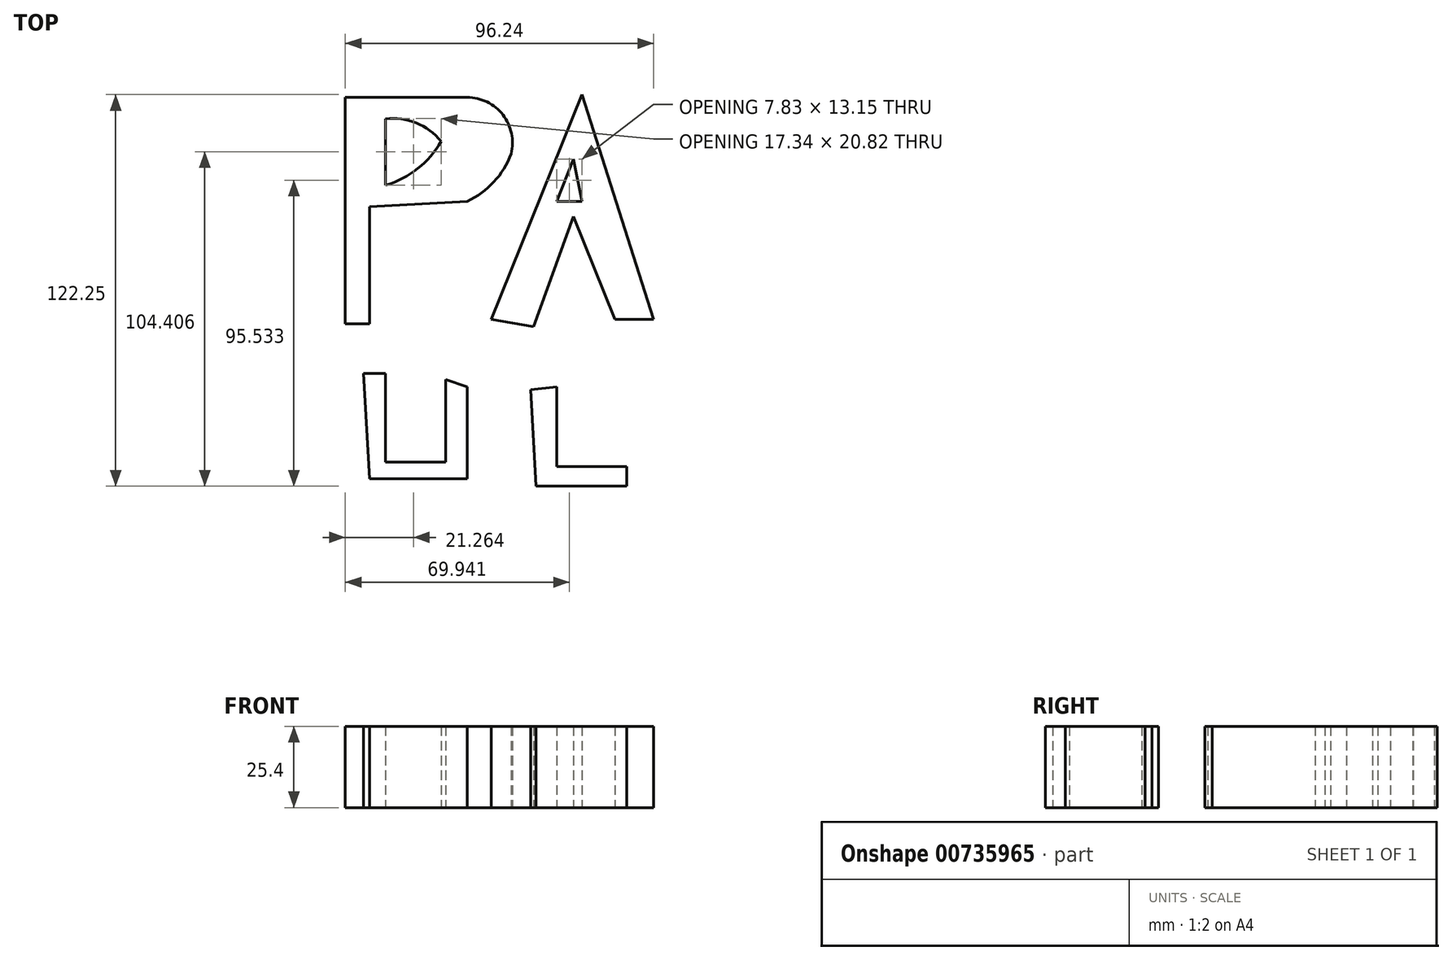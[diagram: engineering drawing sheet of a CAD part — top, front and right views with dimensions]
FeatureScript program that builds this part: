
annotation { "Feature Type Name" : "Feature", "Feature Type Description" : "" }
export const myFeature = defineFeature(function(context is Context, id is Id, definition is map)
    precondition{}
    {
        {
            var Q0;
            Q0=qCreatedBy(makeId("Top.planeOp"),FACE);
            var sketch = newSketch(context, id + "F0", { "sketchPlane" : qUnion([Q0])});
            skLineSegment(sketch, "E0", {"start": v(-71.2, 45.74) * mm, "end": v(-71.2, -25.04) * mm});
            skLineSegment(sketch, "E1", {"start": v(-71.2, -25.04) * mm, "end": v(-63.64, -25.04) * mm});
            skLineSegment(sketch, "E2", {"start": v(-63.64, -25.04) * mm, "end": v(-63.64, 11.6) * mm});
            skLineSegment(sketch, "E3", {"start": v(-71.2, 45.74) * mm, "end": v(-33.15, 45.74) * mm});
            skArc(sketch, "E4", {"start": v(-19.44, 28.12) * mm, "mid": v(-21.99, 40.28) * mm, "end": v(-33.15, 45.74) * mm});
            skArc(sketch, "E5", {"start": v(-33.15, 13.29) * mm, "mid": v(-24.8, 19.32) * mm, "end": v(-19.44, 28.12) * mm});
            skLineSegment(sketch, "E6", {"start": v(-63.64, 11.6) * mm, "end": v(-33.15, 13.29) * mm});
            skLineSegment(sketch, "E7", {"start": v(2.66, 46.58) * mm, "end": v(-25.6, -23.64) * mm});
            skLineSegment(sketch, "E8", {"start": v(-25.6, -23.64) * mm, "end": v(-12.45, -25.88) * mm});
            skLineSegment(sketch, "E9", {"start": v(-12.45, -25.88) * mm, "end": v(0, 8.53) * mm});
            skLineSegment(sketch, "E10", {"start": v(0, 8.53) * mm, "end": v(13, -23.64) * mm});
            skLineSegment(sketch, "E11", {"start": v(13, -23.64) * mm, "end": v(25.04, -23.64) * mm});
            skLineSegment(sketch, "E12", {"start": v(25.04, -23.64) * mm, "end": v(2.66, 46.58) * mm});
            skLineSegment(sketch, "E13", {"start": v(0, 26.44) * mm, "end": v(-5.18, 13.29) * mm});
            skLineSegment(sketch, "E14", {"start": v(-5.18, 13.29) * mm, "end": v(2.66, 13.29) * mm});
            skLineSegment(sketch, "E15", {"start": v(2.66, 13.29) * mm, "end": v(0, 26.44) * mm});
            skLineSegment(sketch, "E16", {"start": v(-58.6, -40.42) * mm, "end": v(-58.6, -68.12) * mm});
            skLineSegment(sketch, "E17", {"start": v(-58.6, -68.12) * mm, "end": v(-39.87, -68.12) * mm});
            skLineSegment(sketch, "E18", {"start": v(-39.87, -68.12) * mm, "end": v(-39.87, -42.38) * mm});
            skLineSegment(sketch, "E19", {"start": v(-5.18, -44.62) * mm, "end": v(-5.18, -69.52) * mm});
            skLineSegment(sketch, "E20", {"start": v(-5.18, -69.52) * mm, "end": v(16.65, -69.52) * mm});
            skLineSegment(sketch, "E21", {"start": v(16.65, -69.52) * mm, "end": v(16.65, -75.67) * mm});
            skLineSegment(sketch, "E22", {"start": v(16.65, -75.67) * mm, "end": v(-11.6, -75.67) * mm});
            skLineSegment(sketch, "E23", {"start": v(-11.6, -75.67) * mm, "end": v(-13.28, -45.54) * mm});
            skLineSegment(sketch, "E24", {"start": v(-13.28, -45.54) * mm, "end": v(-5.18, -44.62) * mm});
            skLineSegment(sketch, "E25", {"start": v(-39.87, -42.38) * mm, "end": v(-33.15, -44.62) * mm});
            skLineSegment(sketch, "E26", {"start": v(-33.15, -44.62) * mm, "end": v(-33.15, -73.44) * mm});
            skLineSegment(sketch, "E27", {"start": v(-33.15, -73.44) * mm, "end": v(-63.64, -73.44) * mm});
            skLineSegment(sketch, "E28", {"start": v(-63.64, -73.44) * mm, "end": v(-65.53, -40.42) * mm});
            skLineSegment(sketch, "E29", {"start": v(-65.53, -40.42) * mm, "end": v(-58.6, -40.42) * mm});
            skLineSegment(sketch, "E30", {"start": v(-58.6, 39.03) * mm, "end": v(-58.6, 18.32) * mm});
            skArc(sketch, "E31", {"start": v(-41.26, 32.03) * mm, "mid": v(-49.05, 37.72) * mm, "end": v(-58.6, 39.03) * mm});
            skArc(sketch, "E32", {"start": v(-58.6, 18.32) * mm, "mid": v(-48.59, 23.47) * mm, "end": v(-41.26, 32.03) * mm});
            skSolve(sketch);
        }
        {
            var Q0;
            Q0 = qSketchRegion(id + "F0", true);
            extrude(context, id + "F1", {"entities" : qUnion([Q0]), "depth" : 25.4 * mm, "offsetDistance" : 25.4 * mm});
        }
    });
